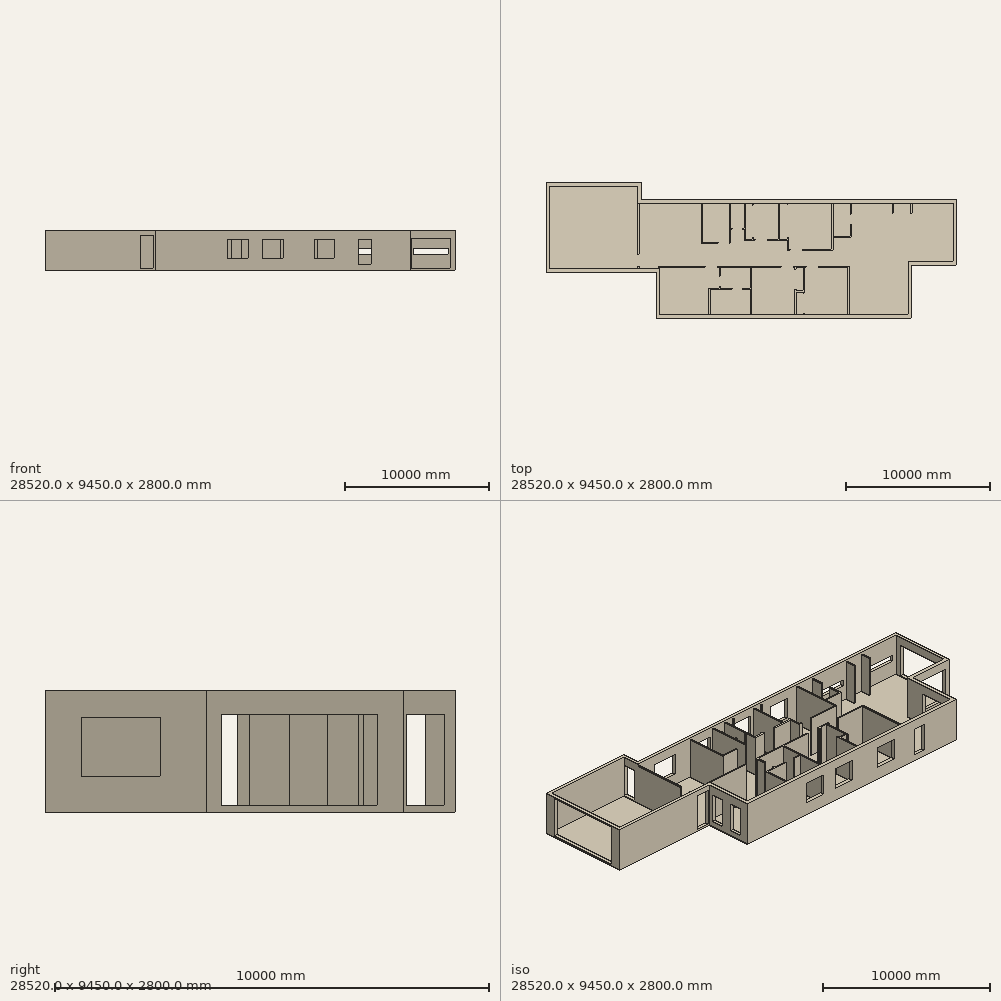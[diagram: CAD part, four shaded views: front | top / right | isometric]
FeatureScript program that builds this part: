
annotation { "Feature Type Name" : "Feature", "Feature Type Description" : "" }
export const myFeature = defineFeature(function(context is Context, id is Id, definition is map)
    precondition{}
    {
        {
            var Q0;
            Q0=qCreatedBy(makeId("Top.planeOp"),FACE);
            var sketch = newSketch(context, id + "F0", { "sketchPlane" : qUnion([Q0])});
            skLineSegment(sketch, "E0.bottom", {"start": v(-9337.55, 6230) * mm, "end": v(-2747.55, 6230) * mm});
            skLineSegment(sketch, "E0.top", {"start": v(-9337.55, 0) * mm, "end": v(-2747.55, 0) * mm});
            skLineSegment(sketch, "E0.left", {"start": v(-9337.55, 6230) * mm, "end": v(-9337.55, 0) * mm});
            skLineSegment(sketch, "E0.right", {"start": v(-2747.55, 6230) * mm, "end": v(-2747.55, 5040) * mm});
            skLineSegment(sketch, "E1.bottom", {"start": v(-2747.55, 5040) * mm, "end": v(19182.45, 5040) * mm});
            skLineSegment(sketch, "E1.top", {"start": v(16062.45, 490) * mm, "end": v(19182.45, 490) * mm});
            skLineSegment(sketch, "E1.right", {"start": v(19182.45, 5040) * mm, "end": v(19182.45, 490) * mm});
            skLineSegment(sketch, "E2.top", {"start": v(-1687.55, -3220) * mm, "end": v(16062.45, -3220) * mm});
            skLineSegment(sketch, "E2.left", {"start": v(-1687.55, 490) * mm, "end": v(-1687.55, -3220) * mm});
            skLineSegment(sketch, "E2.right", {"start": v(16062.45, 490) * mm, "end": v(16062.45, -3220) * mm});
            skLineSegment(sketch, "E3", {"start": v(-2747.55, 0) * mm, "end": v(-1687.55, 0) * mm});
            skLineSegment(sketch, "E4.bottom", {"start": v(19182.45, 5040) * mm, "end": v(22182.45, 5040) * mm});
            skLineSegment(sketch, "E4.top", {"start": v(19182.45, -3220) * mm, "end": v(22182.45, -3220) * mm});
            skLineSegment(sketch, "E4.right", {"start": v(22182.45, 5040) * mm, "end": v(22182.45, -3220) * mm});
            skLineSegment(sketch, "E5.top", {"start": v(16062.45, -3220) * mm, "end": v(19182.45, -3220) * mm});
            skSolve(sketch);
        }
        {
            var Q0;
            Q0=makeQuery(id+"F0.imprint","IMPRINT",FACE,{"disambiguationData":[TD([[makeQuery(id+"F0.imprint","IMPRINT",EDGE,{"derivedFrom":sQuery(id+"F0.wireOp",EDGE,"E0.bottom")}),-1.0]])]});
            extrude(context, id + "F1", {"entities" : qUnion([Q0]), "depth" : 5 * mm});
        }
        {
            var Q0;
            Q0=makeQuery(id+"F1.opExtrude","CAP_FACE",FACE,{"disambiguationData":[OSD([sQuery(id+"F0.wireOp",EDGE,"E0.bottom"),sQuery(id+"F0.wireOp",EDGE,"E0.top"),sQuery(id+"F0.wireOp",EDGE,"E0.left"),sQuery(id+"F0.wireOp",EDGE,"E0.right"),sQuery(id+"F0.wireOp",EDGE,"E1.bottom"),sQuery(id+"F0.wireOp",EDGE,"E2.top"),sQuery(id+"F0.wireOp",EDGE,"E2.left"),sQuery(id+"F0.wireOp",EDGE,"E3"),sQuery(id+"F0.wireOp",EDGE,"E1.right"),sQuery(id+"F0.wireOp",EDGE,"E1.top"),sQuery(id+"F0.wireOp",EDGE,"E2.right")])],"isStart":false});
            var sketch = newSketch(context, id + "F2", { "sketchPlane" : qUnion([Q0])});
            skLineSegment(sketch, "E6.bottom", {"start": v(-9337.55, 6230) * mm, "end": v(-2747.55, 6230) * mm});
            skLineSegment(sketch, "E6.top", {"start": v(-9097.55, 5990) * mm, "end": v(-2987.55, 5990) * mm});
            skLineSegment(sketch, "E6.left", {"start": v(-9337.55, 6230) * mm, "end": v(-9337.55, 5990) * mm});
            skLineSegment(sketch, "E6.right", {"start": v(-2747.55, 6230) * mm, "end": v(-2747.55, 5990) * mm});
            skLineSegment(sketch, "E7.left", {"start": v(-2987.55, 5990) * mm, "end": v(-2987.55, 5040) * mm});
            skLineSegment(sketch, "E7.right", {"start": v(-2747.55, 5990) * mm, "end": v(-2747.55, 5040) * mm});
            skLineSegment(sketch, "E8.bottom", {"start": v(-2747.55, 5040) * mm, "end": v(19182.45, 5040) * mm});
            skLineSegment(sketch, "E8.top", {"start": v(-2987.55, 4800) * mm, "end": v(19182.45, 4800) * mm});
            skLineSegment(sketch, "E8.left", {"start": v(-2987.55, 5040) * mm, "end": v(-2987.55, 4800) * mm});
            skLineSegment(sketch, "E8.right", {"start": v(19182.45, 5040) * mm, "end": v(19182.45, 4800) * mm});
            skLineSegment(sketch, "E9.bottom", {"start": v(18942.45, 4800) * mm, "end": v(19182.45, 4800) * mm});
            skLineSegment(sketch, "E9.top", {"start": v(18942.45, 490) * mm, "end": v(19182.45, 490) * mm});
            skLineSegment(sketch, "E9.left", {"start": v(18942.45, 4800) * mm, "end": v(18942.45, 730) * mm});
            skLineSegment(sketch, "E9.right", {"start": v(19182.45, 4800) * mm, "end": v(19182.45, 490) * mm});
            skLineSegment(sketch, "E10.bottom", {"start": v(16062.45, 490) * mm, "end": v(18942.45, 490) * mm});
            skLineSegment(sketch, "E10.top", {"start": v(16062.45, 730) * mm, "end": v(18942.45, 730) * mm});
            skLineSegment(sketch, "E11.bottom", {"start": v(16062.45, 730) * mm, "end": v(15822.45, 730) * mm});
            skLineSegment(sketch, "E11.top", {"start": v(16062.45, -3220) * mm, "end": v(15822.45, -3220) * mm});
            skLineSegment(sketch, "E11.left", {"start": v(16062.45, 490) * mm, "end": v(16062.45, -3220) * mm});
            skLineSegment(sketch, "E11.right", {"start": v(15822.45, 730) * mm, "end": v(15822.45, -2980) * mm});
            skLineSegment(sketch, "E12.bottom", {"start": v(15822.45, -3220) * mm, "end": v(-1687.55, -3220) * mm});
            skLineSegment(sketch, "E12.top", {"start": v(15822.45, -2980) * mm, "end": v(-1447.55, -2980) * mm});
            skLineSegment(sketch, "E12.right", {"start": v(-1687.55, -3220) * mm, "end": v(-1687.55, -2980) * mm});
            skLineSegment(sketch, "E13.left", {"start": v(-1687.55, -2980) * mm, "end": v(-1687.55, 0) * mm});
            skLineSegment(sketch, "E13.right", {"start": v(-1447.55, -2980) * mm, "end": v(-1447.55, 0) * mm});
            skLineSegment(sketch, "E14.bottom", {"start": v(-1687.55, 0) * mm, "end": v(-9337.55, 0) * mm});
            skLineSegment(sketch, "E14.top", {"start": v(-1447.55, 240) * mm, "end": v(-9097.55, 240) * mm});
            skLineSegment(sketch, "E14.left", {"start": v(-1447.55, 0) * mm, "end": v(-1447.55, 240) * mm});
            skLineSegment(sketch, "E14.right", {"start": v(-9337.55, 0) * mm, "end": v(-9337.55, 240) * mm});
            skLineSegment(sketch, "E15.left", {"start": v(-9337.55, 240) * mm, "end": v(-9337.55, 5990) * mm});
            skLineSegment(sketch, "E15.right", {"start": v(-9097.55, 240) * mm, "end": v(-9097.55, 5990) * mm});
            skSolve(sketch);
        }
        {
            var Q0;
            Q0=makeQuery(id+"F2.imprint","IMPRINT",FACE,{"disambiguationData":[TD([[makeQuery(id+"F2.imprint","IMPRINT",EDGE,{"derivedFrom":sQuery(id+"F2.wireOp",EDGE,"E6.bottom")}),-1.0]])]});
            extrude(context, id + "F3", {"entities" : qUnion([Q0]), "operationType" : NewBodyOperationType.ADD, "depth" : 2700 * mm});
        }
        {
            var Q0;
            Q0=makeQuery(id+"F1.opExtrude","CAP_FACE",FACE,{"disambiguationData":[OSD([sQuery(id+"F0.wireOp",EDGE,"E0.bottom"),sQuery(id+"F0.wireOp",EDGE,"E0.top"),sQuery(id+"F0.wireOp",EDGE,"E0.left"),sQuery(id+"F0.wireOp",EDGE,"E0.right"),sQuery(id+"F0.wireOp",EDGE,"E1.bottom"),sQuery(id+"F0.wireOp",EDGE,"E2.top"),sQuery(id+"F0.wireOp",EDGE,"E2.left"),sQuery(id+"F0.wireOp",EDGE,"E3"),sQuery(id+"F0.wireOp",EDGE,"E1.right"),sQuery(id+"F0.wireOp",EDGE,"E1.top"),sQuery(id+"F0.wireOp",EDGE,"E2.right")])],"isStart":false});
            var sketch = newSketch(context, id + "F4", { "sketchPlane" : qUnion([Q0])});
            skLineSegment(sketch, "E16.bottom", {"start": v(-2987.55, 4800) * mm, "end": v(-2897.55, 4800) * mm});
            skLineSegment(sketch, "E16.top", {"start": v(-2987.55, 1210) * mm, "end": v(-2897.55, 1210) * mm});
            skLineSegment(sketch, "E16.left", {"start": v(-2987.55, 4800) * mm, "end": v(-2987.55, 1210) * mm});
            skLineSegment(sketch, "E16.right", {"start": v(-2897.55, 4800) * mm, "end": v(-2897.55, 1210) * mm});
            skLineSegment(sketch, "E17.bottom", {"start": v(1442.45, 4800) * mm, "end": v(1532.45, 4800) * mm});
            skLineSegment(sketch, "E17.top", {"start": v(1442.45, 2000) * mm, "end": v(1532.45, 2000) * mm});
            skLineSegment(sketch, "E17.left", {"start": v(1442.45, 4800) * mm, "end": v(1442.45, 2000) * mm});
            skLineSegment(sketch, "E17.right", {"start": v(1532.45, 4800) * mm, "end": v(1532.45, 2090) * mm});
            skLineSegment(sketch, "E18.bottom", {"start": v(-2987.55, 240) * mm, "end": v(-2897.55, 240) * mm});
            skLineSegment(sketch, "E18.top", {"start": v(-2987.55, 390) * mm, "end": v(-2897.55, 390) * mm});
            skLineSegment(sketch, "E18.left", {"start": v(-2987.55, 240) * mm, "end": v(-2987.55, 390) * mm});
            skLineSegment(sketch, "E18.right", {"start": v(-2897.55, 240) * mm, "end": v(-2897.55, 390) * mm});
            skLineSegment(sketch, "E19.bottom", {"start": v(3362.45, 4800) * mm, "end": v(3452.45, 4800) * mm});
            skLineSegment(sketch, "E19.top", {"start": v(3362.45, 2000) * mm, "end": v(3452.45, 2000) * mm});
            skLineSegment(sketch, "E19.left", {"start": v(3362.45, 4800) * mm, "end": v(3362.45, 2000) * mm});
            skLineSegment(sketch, "E19.right", {"start": v(3452.45, 4800) * mm, "end": v(3452.45, 3030) * mm});
            skLineSegment(sketch, "E20.bottom", {"start": v(1532.45, 2000) * mm, "end": v(2642.45, 2000) * mm});
            skLineSegment(sketch, "E20.top", {"start": v(1532.45, 2090) * mm, "end": v(2642.45, 2090) * mm});
            skLineSegment(sketch, "E20.right", {"start": v(2642.45, 2000) * mm, "end": v(2642.45, 2090) * mm});
            skLineSegment(sketch, "E21.bottom", {"start": v(4402.45, 4800) * mm, "end": v(4492.45, 4800) * mm});
            skLineSegment(sketch, "E21.left", {"start": v(4402.45, 4800) * mm, "end": v(4402.45, 3030) * mm});
            skLineSegment(sketch, "E21.right", {"start": v(4492.45, 4800) * mm, "end": v(4492.45, 2940) * mm});
            skLineSegment(sketch, "E22.bottom", {"start": v(4402.45, 2940) * mm, "end": v(4287.45, 2940) * mm});
            skLineSegment(sketch, "E22.top", {"start": v(4402.45, 3030) * mm, "end": v(4287.45, 3030) * mm});
            skLineSegment(sketch, "E22.right", {"start": v(4287.45, 2940) * mm, "end": v(4287.45, 3030) * mm});
            skLineSegment(sketch, "E23.bottom", {"start": v(3452.45, 3030) * mm, "end": v(3567.45, 3030) * mm});
            skLineSegment(sketch, "E23.top", {"start": v(3452.45, 2940) * mm, "end": v(3567.45, 2940) * mm});
            skLineSegment(sketch, "E23.right", {"start": v(3567.45, 3030) * mm, "end": v(3567.45, 2940) * mm});
            skLineSegment(sketch, "E24.trimOffspring", {"start": v(3452.45, 2940) * mm, "end": v(3452.45, 2000) * mm});
            skLineSegment(sketch, "E25.bottom", {"start": v(5002.45, 4800) * mm, "end": v(5092.45, 4800) * mm});
            skLineSegment(sketch, "E25.top", {"start": v(5002.45, 4650) * mm, "end": v(5092.45, 4650) * mm});
            skLineSegment(sketch, "E25.left", {"start": v(5002.45, 4800) * mm, "end": v(5002.45, 4650) * mm});
            skLineSegment(sketch, "E25.right", {"start": v(5092.45, 4800) * mm, "end": v(5092.45, 4650) * mm});
            skLineSegment(sketch, "E26.bottom", {"start": v(-1447.55, 240) * mm, "end": v(-1537.55, 240) * mm});
            skLineSegment(sketch, "E26.top", {"start": v(-1447.55, 390) * mm, "end": v(-1537.55, 390) * mm});
            skLineSegment(sketch, "E26.left", {"start": v(-1447.55, 240) * mm, "end": v(-1447.55, 300) * mm});
            skLineSegment(sketch, "E26.right", {"start": v(-1537.55, 240) * mm, "end": v(-1537.55, 390) * mm});
            skLineSegment(sketch, "E27.bottom", {"start": v(-1447.55, 390) * mm, "end": v(1727.45, 390) * mm});
            skLineSegment(sketch, "E27.top", {"start": v(-1447.55, 300) * mm, "end": v(1727.45, 300) * mm});
            skLineSegment(sketch, "E27.right", {"start": v(1727.45, 390) * mm, "end": v(1727.45, 300) * mm});
            skLineSegment(sketch, "E28.bottom", {"start": v(1952.45, -2980) * mm, "end": v(2042.45, -2980) * mm});
            skLineSegment(sketch, "E28.left", {"start": v(1952.45, -2980) * mm, "end": v(1952.45, -1210) * mm});
            skLineSegment(sketch, "E28.right", {"start": v(2042.45, -2980) * mm, "end": v(2042.45, -1210) * mm});
            skLineSegment(sketch, "E29.bottom", {"start": v(4852.45, -2980) * mm, "end": v(4942.45, -2980) * mm});
            skLineSegment(sketch, "E29.top", {"start": v(4852.45, 300) * mm, "end": v(4942.45, 300) * mm});
            skLineSegment(sketch, "E29.left", {"start": v(4852.45, -2980) * mm, "end": v(4852.45, 300) * mm});
            skLineSegment(sketch, "E29.right", {"start": v(4942.45, -2980) * mm, "end": v(4942.45, 300) * mm});
            skLineSegment(sketch, "E30.bottom", {"start": v(2042.45, -1210) * mm, "end": v(3582.45, -1210) * mm});
            skLineSegment(sketch, "E30.top", {"start": v(1952.45, -1120) * mm, "end": v(3582.45, -1120) * mm});
            skLineSegment(sketch, "E30.left", {"start": v(1952.45, -1210) * mm, "end": v(1952.45, -1120) * mm});
            skLineSegment(sketch, "E30.right", {"start": v(3582.45, -1210) * mm, "end": v(3582.45, -1120) * mm});
            skLineSegment(sketch, "E31.bottom", {"start": v(4852.45, -1210) * mm, "end": v(4302.45, -1210) * mm});
            skLineSegment(sketch, "E31.top", {"start": v(4852.45, -1120) * mm, "end": v(4302.45, -1120) * mm});
            skLineSegment(sketch, "E31.left", {"start": v(4852.45, -1210) * mm, "end": v(4852.45, -1120) * mm});
            skLineSegment(sketch, "E31.right", {"start": v(4302.45, -1210) * mm, "end": v(4302.45, -1120) * mm});
            skLineSegment(sketch, "E32.bottom", {"start": v(4942.45, 300) * mm, "end": v(2752.45, 300) * mm});
            skLineSegment(sketch, "E32.top", {"start": v(4942.45, 390) * mm, "end": v(2752.45, 390) * mm});
            skLineSegment(sketch, "E32.left", {"start": v(4942.45, 300) * mm, "end": v(4942.45, 390) * mm});
            skLineSegment(sketch, "E33.bottom", {"start": v(2752.45, 390) * mm, "end": v(2662.45, 390) * mm});
            skLineSegment(sketch, "E33.top", {"start": v(2752.45, -285) * mm, "end": v(2662.45, -285) * mm});
            skLineSegment(sketch, "E33.left", {"start": v(2752.45, 300) * mm, "end": v(2752.45, -285) * mm});
            skLineSegment(sketch, "E33.right", {"start": v(2662.45, 300) * mm, "end": v(2662.45, -285) * mm});
            skLineSegment(sketch, "E34.bottom", {"start": v(2662.45, -1120) * mm, "end": v(2752.45, -1120) * mm});
            skLineSegment(sketch, "E34.top", {"start": v(2662.45, -1005) * mm, "end": v(2752.45, -1005) * mm});
            skLineSegment(sketch, "E34.left", {"start": v(2662.45, -1120) * mm, "end": v(2662.45, -1005) * mm});
            skLineSegment(sketch, "E34.right", {"start": v(2752.45, -1120) * mm, "end": v(2752.45, -1005) * mm});
            skLineSegment(sketch, "E35.bottom", {"start": v(2662.45, 390) * mm, "end": v(2547.45, 390) * mm});
            skLineSegment(sketch, "E35.top", {"start": v(2662.45, 300) * mm, "end": v(2547.45, 300) * mm});
            skLineSegment(sketch, "E35.right", {"start": v(2547.45, 390) * mm, "end": v(2547.45, 300) * mm});
            skLineSegment(sketch, "E36.bottom", {"start": v(7942.45, -2980) * mm, "end": v(8032.45, -2980) * mm});
            skLineSegment(sketch, "E36.top", {"start": v(7942.45, -1180) * mm, "end": v(8032.45, -1180) * mm});
            skLineSegment(sketch, "E36.left", {"start": v(7942.45, -2980) * mm, "end": v(7942.45, -1180) * mm});
            skLineSegment(sketch, "E36.right", {"start": v(8032.45, -2980) * mm, "end": v(8032.45, -1385) * mm});
            skLineSegment(sketch, "E37.bottom", {"start": v(8032.45, -1295) * mm, "end": v(8542.45, -1295) * mm});
            skLineSegment(sketch, "E37.top", {"start": v(8032.45, -1385) * mm, "end": v(8542.45, -1385) * mm});
            skLineSegment(sketch, "E38.bottom", {"start": v(8542.45, -1500) * mm, "end": v(8632.45, -1500) * mm});
            skLineSegment(sketch, "E38.left", {"start": v(8542.45, -1500) * mm, "end": v(8542.45, -1385) * mm});
            skLineSegment(sketch, "E38.right", {"start": v(8632.45, -1500) * mm, "end": v(8632.45, 300) * mm});
            skLineSegment(sketch, "E39.bottom", {"start": v(4942.45, 390) * mm, "end": v(7007.45, 390) * mm});
            skLineSegment(sketch, "E39.top", {"start": v(4942.45, 300) * mm, "end": v(7007.45, 300) * mm});
            skLineSegment(sketch, "E39.left", {"start": v(4942.45, 390) * mm, "end": v(4942.45, 300) * mm});
            skLineSegment(sketch, "E39.right", {"start": v(7007.45, 390) * mm, "end": v(7007.45, 300) * mm});
            skLineSegment(sketch, "E40.bottom", {"start": v(8542.45, 300) * mm, "end": v(8032.45, 300) * mm});
            skLineSegment(sketch, "E40.top", {"start": v(8632.45, 390) * mm, "end": v(7827.45, 390) * mm});
            skLineSegment(sketch, "E40.right", {"start": v(7827.45, 300) * mm, "end": v(7827.45, 390) * mm});
            skLineSegment(sketch, "E41.top", {"start": v(7942.45, 185) * mm, "end": v(8032.45, 185) * mm});
            skLineSegment(sketch, "E41.left", {"start": v(7942.45, 300) * mm, "end": v(7942.45, 185) * mm});
            skLineSegment(sketch, "E41.right", {"start": v(8032.45, 300) * mm, "end": v(8032.45, 185) * mm});
            skLineSegment(sketch, "E42.trimOffspring", {"start": v(7942.45, 300) * mm, "end": v(7827.45, 300) * mm});
            skLineSegment(sketch, "E43.trimOffspring", {"start": v(8542.45, -1295) * mm, "end": v(8542.45, 300) * mm});
            skLineSegment(sketch, "E44.trimOffspring", {"start": v(8032.45, -1295) * mm, "end": v(8032.45, -1180) * mm});
            skLineSegment(sketch, "E45.bottom", {"start": v(8542.45, -2980) * mm, "end": v(8632.45, -2980) * mm});
            skLineSegment(sketch, "E45.top", {"start": v(8542.45, -2865) * mm, "end": v(8632.45, -2865) * mm});
            skLineSegment(sketch, "E45.left", {"start": v(8542.45, -2980) * mm, "end": v(8542.45, -2865) * mm});
            skLineSegment(sketch, "E45.right", {"start": v(8632.45, -2980) * mm, "end": v(8632.45, -2865) * mm});
            skLineSegment(sketch, "E46.bottom", {"start": v(8632.45, 300) * mm, "end": v(8747.45, 300) * mm});
            skLineSegment(sketch, "E46.top", {"start": v(8632.45, 390) * mm, "end": v(8747.45, 390) * mm});
            skLineSegment(sketch, "E46.right", {"start": v(8747.45, 300) * mm, "end": v(8747.45, 390) * mm});
            skLineSegment(sketch, "E47.bottom", {"start": v(11632.45, -2980) * mm, "end": v(11722.45, -2980) * mm});
            skLineSegment(sketch, "E47.left", {"start": v(11632.45, -2980) * mm, "end": v(11632.45, 300) * mm});
            skLineSegment(sketch, "E47.right", {"start": v(11722.45, -2980) * mm, "end": v(11722.45, 300) * mm});
            skLineSegment(sketch, "E48.bottom", {"start": v(11632.45, 300) * mm, "end": v(9567.45, 300) * mm});
            skLineSegment(sketch, "E48.top", {"start": v(11722.45, 390) * mm, "end": v(9567.45, 390) * mm});
            skLineSegment(sketch, "E48.left", {"start": v(11722.45, 300) * mm, "end": v(11722.45, 390) * mm});
            skLineSegment(sketch, "E48.right", {"start": v(9567.45, 300) * mm, "end": v(9567.45, 390) * mm});
            skLineSegment(sketch, "E49.bottom", {"start": v(16002.45, 4800) * mm, "end": v(16092.45, 4800) * mm});
            skLineSegment(sketch, "E49.top", {"start": v(16002.45, 4100) * mm, "end": v(16092.45, 4100) * mm});
            skLineSegment(sketch, "E49.left", {"start": v(16002.45, 4800) * mm, "end": v(16002.45, 4100) * mm});
            skLineSegment(sketch, "E49.right", {"start": v(16092.45, 4800) * mm, "end": v(16092.45, 4100) * mm});
            skLineSegment(sketch, "E50.bottom", {"start": v(14712.45, 4800) * mm, "end": v(14802.45, 4800) * mm});
            skLineSegment(sketch, "E50.top", {"start": v(14712.45, 4100) * mm, "end": v(14802.45, 4100) * mm});
            skLineSegment(sketch, "E50.left", {"start": v(14712.45, 4800) * mm, "end": v(14712.45, 4100) * mm});
            skLineSegment(sketch, "E50.right", {"start": v(14802.45, 4800) * mm, "end": v(14802.45, 4100) * mm});
            skLineSegment(sketch, "E51.bottom", {"start": v(11802.45, 4800) * mm, "end": v(11892.45, 4800) * mm});
            skLineSegment(sketch, "E51.top", {"start": v(11802.45, 4005) * mm, "end": v(11892.45, 4005) * mm});
            skLineSegment(sketch, "E51.left", {"start": v(11802.45, 4800) * mm, "end": v(11802.45, 4005) * mm});
            skLineSegment(sketch, "E51.right", {"start": v(11892.45, 4800) * mm, "end": v(11892.45, 4005) * mm});
            skLineSegment(sketch, "E52.bottom", {"start": v(11802.45, 3285) * mm, "end": v(11892.45, 3285) * mm});
            skLineSegment(sketch, "E52.left", {"start": v(11802.45, 3285) * mm, "end": v(11802.45, 2490) * mm});
            skLineSegment(sketch, "E52.right", {"start": v(11892.45, 3285) * mm, "end": v(11892.45, 2490) * mm});
            skLineSegment(sketch, "E53.bottom", {"start": v(11802.45, 2490) * mm, "end": v(10602.45, 2490) * mm});
            skLineSegment(sketch, "E53.top", {"start": v(11892.45, 2400) * mm, "end": v(10602.45, 2400) * mm});
            skLineSegment(sketch, "E53.left", {"start": v(11892.45, 2490) * mm, "end": v(11892.45, 2400) * mm});
            skLineSegment(sketch, "E54.top", {"start": v(10602.45, 4800) * mm, "end": v(10512.45, 4800) * mm});
            skLineSegment(sketch, "E54.left", {"start": v(10602.45, 1570) * mm, "end": v(10602.45, 2400) * mm});
            skLineSegment(sketch, "E54.right", {"start": v(10512.45, 1570) * mm, "end": v(10512.45, 4800) * mm});
            skLineSegment(sketch, "E55.trimOffspring", {"start": v(10602.45, 2490) * mm, "end": v(10602.45, 4800) * mm});
            skLineSegment(sketch, "E56.bottom", {"start": v(10512.45, 1570) * mm, "end": v(8452.45, 1570) * mm});
            skLineSegment(sketch, "E56.top", {"start": v(10602.45, 1480) * mm, "end": v(8452.45, 1480) * mm});
            skLineSegment(sketch, "E56.left", {"start": v(10602.45, 1570) * mm, "end": v(10602.45, 1480) * mm});
            skLineSegment(sketch, "E56.right", {"start": v(8452.45, 1570) * mm, "end": v(8452.45, 1480) * mm});
            skLineSegment(sketch, "E57.bottom", {"start": v(7482.45, 4800) * mm, "end": v(7392.45, 4800) * mm});
            skLineSegment(sketch, "E57.top", {"start": v(7482.45, 4685) * mm, "end": v(7392.45, 4685) * mm});
            skLineSegment(sketch, "E57.left", {"start": v(7482.45, 4800) * mm, "end": v(7482.45, 4685) * mm});
            skLineSegment(sketch, "E57.right", {"start": v(7392.45, 4800) * mm, "end": v(7392.45, 4685) * mm});
            skLineSegment(sketch, "E58.bottom", {"start": v(7632.45, 1570) * mm, "end": v(7482.45, 1570) * mm});
            skLineSegment(sketch, "E58.top", {"start": v(7632.45, 1480) * mm, "end": v(7482.45, 1480) * mm});
            skLineSegment(sketch, "E58.left", {"start": v(7632.45, 1570) * mm, "end": v(7632.45, 1480) * mm});
            skLineSegment(sketch, "E58.right", {"start": v(7482.45, 1570) * mm, "end": v(7482.45, 1480) * mm});
            skLineSegment(sketch, "E59.bottom", {"start": v(7482.45, 1480) * mm, "end": v(7392.45, 1480) * mm});
            skLineSegment(sketch, "E59.top", {"start": v(7482.45, 2415) * mm, "end": v(7392.45, 2415) * mm});
            skLineSegment(sketch, "E59.left", {"start": v(7482.45, 1480) * mm, "end": v(7482.45, 2415) * mm});
            skLineSegment(sketch, "E59.right", {"start": v(7392.45, 1480) * mm, "end": v(7392.45, 2210) * mm});
            skLineSegment(sketch, "E60.bottom", {"start": v(6882.45, 4800) * mm, "end": v(6792.45, 4800) * mm});
            skLineSegment(sketch, "E60.top", {"start": v(6882.45, 2210) * mm, "end": v(6792.45, 2210) * mm});
            skLineSegment(sketch, "E60.left", {"start": v(6882.45, 4800) * mm, "end": v(6882.45, 2300) * mm});
            skLineSegment(sketch, "E60.right", {"start": v(6792.45, 4800) * mm, "end": v(6792.45, 2300) * mm});
            skLineSegment(sketch, "E61.bottom", {"start": v(6882.45, 2210) * mm, "end": v(7392.45, 2210) * mm});
            skLineSegment(sketch, "E61.top", {"start": v(6882.45, 2300) * mm, "end": v(7392.45, 2300) * mm});
            skLineSegment(sketch, "E62.trimOffspring", {"start": v(7392.45, 2300) * mm, "end": v(7392.45, 2415) * mm});
            skLineSegment(sketch, "E63.bottom", {"start": v(6792.45, 2210) * mm, "end": v(6027.45, 2210) * mm});
            skLineSegment(sketch, "E63.top", {"start": v(6792.45, 2300) * mm, "end": v(6027.45, 2300) * mm});
            skLineSegment(sketch, "E63.right", {"start": v(6027.45, 2210) * mm, "end": v(6027.45, 2300) * mm});
            skLineSegment(sketch, "E64.top", {"start": v(4402.45, 2210) * mm, "end": v(4492.45, 2210) * mm});
            skLineSegment(sketch, "E64.left", {"start": v(4402.45, 2940) * mm, "end": v(4402.45, 2210) * mm});
            skLineSegment(sketch, "E64.right", {"start": v(4492.45, 2940) * mm, "end": v(4492.45, 2300) * mm});
            skLineSegment(sketch, "E65.bottom", {"start": v(4492.45, 2210) * mm, "end": v(5207.45, 2210) * mm});
            skLineSegment(sketch, "E65.top", {"start": v(4492.45, 2300) * mm, "end": v(5002.45, 2300) * mm});
            skLineSegment(sketch, "E65.right", {"start": v(5207.45, 2210) * mm, "end": v(5207.45, 2300) * mm});
            skPoint(sketch, "E66.oppositeSnap0", {"position": v(5092.45, 4725) * mm});
            skLineSegment(sketch, "E66.top", {"start": v(5002.45, 2415) * mm, "end": v(5092.45, 2415) * mm});
            skLineSegment(sketch, "E66.left", {"start": v(5002.45, 2300) * mm, "end": v(5002.45, 2415) * mm});
            skLineSegment(sketch, "E66.right", {"start": v(5092.45, 2300) * mm, "end": v(5092.45, 2415) * mm});
            skLineSegment(sketch, "E67.trimOffspring", {"start": v(5092.45, 2300) * mm, "end": v(5207.45, 2300) * mm});
            skSolve(sketch);
        }
        {
            var Q0;
            Q0 = qSketchRegion(id + "F4", true);
            extrude(context, id + "F5", {"entities" : qUnion([Q0]), "operationType" : NewBodyOperationType.ADD, "depth" : 2590 * mm});
        }
        {
            var Q0;
            Q0=makeQuery(id+"F3.boolean.opBoolean","MERGE",FACE,{"derivedFrom":[makeQuery(id+"F1.opExtrude","SWEPT_FACE",FACE,{"disambiguationData":[OSD([sQuery(id+"F0.wireOp",EDGE,"E0.left")])]}),makeQuery(id+"F3.opExtrude","SWEPT_FACE",FACE,{"disambiguationData":[OSD([sQuery(id+"F2.wireOp",EDGE,"E6.left"),sQuery(id+"F2.wireOp",EDGE,"E14.right"),sQuery(id+"F2.wireOp",EDGE,"E15.left")])]})]});
            var sketch = newSketch(context, id + "F6", { "sketchPlane" : qUnion([Q0])});
            skLineSegment(sketch, "E68.bottom", {"start": v(-5530, 2620) * mm, "end": v(-700, 2620) * mm});
            skLineSegment(sketch, "E68.top", {"start": v(-5530, 30) * mm, "end": v(-700, 30) * mm});
            skLineSegment(sketch, "E68.left", {"start": v(-5530, 2620) * mm, "end": v(-5530, 30) * mm});
            skLineSegment(sketch, "E68.right", {"start": v(-700, 2620) * mm, "end": v(-700, 30) * mm});
            skSolve(sketch);
        }
        {
            var Q0;
            Q0=makeQuery(id+"F6.imprint","IMPRINT",FACE,{"disambiguationData":[TD([[makeQuery(id+"F6.imprint","IMPRINT",EDGE,{"derivedFrom":sQuery(id+"F6.wireOp",EDGE,"E68.bottom")}),-1.0]])]});
            extrude(context, id + "F7", {"entities" : qUnion([Q0]), "operationType" : NewBodyOperationType.REMOVE, "oppositeDirection" : true, "depth" : 400 * mm});
        }
        {
            var Q0;
            Q0=makeQuery(id+"F3.boolean.opBoolean","MERGE",FACE,{"derivedFrom":[makeQuery(id+"F1.opExtrude","SWEPT_FACE",FACE,{"disambiguationData":[OSD([sQuery(id+"F0.wireOp",EDGE,"E0.top"),sQuery(id+"F0.wireOp",EDGE,"E3")])]}),makeQuery(id+"F3.opExtrude","SWEPT_FACE",FACE,{"disambiguationData":[OSD([sQuery(id+"F2.wireOp",EDGE,"E14.bottom")])]})]});
            var sketch = newSketch(context, id + "F8", { "sketchPlane" : qUnion([Q0])});
            skLineSegment(sketch, "E69.bottom", {"start": v(-2722.55, 2370) * mm, "end": v(-1802.55, 2370) * mm});
            skLineSegment(sketch, "E69.top", {"start": v(-2722.55, 30) * mm, "end": v(-1802.55, 30) * mm});
            skLineSegment(sketch, "E69.left", {"start": v(-2722.55, 2370) * mm, "end": v(-2722.55, 30) * mm});
            skLineSegment(sketch, "E69.right", {"start": v(-1802.55, 2370) * mm, "end": v(-1802.55, 30) * mm});
            skSolve(sketch);
        }
        {
            var Q0;
            Q0=makeQuery(id+"F8.imprint","IMPRINT",FACE,{"disambiguationData":[TD([[makeQuery(id+"F8.imprint","IMPRINT",EDGE,{"derivedFrom":sQuery(id+"F8.wireOp",EDGE,"E69.bottom")}),-1.0]])]});
            extrude(context, id + "F9", {"entities" : qUnion([Q0]), "operationType" : NewBodyOperationType.REMOVE, "oppositeDirection" : true, "depth" : 400 * mm});
        }
        {
            var Q0;
            Q0=makeQuery(id+"F3.boolean.opBoolean","MERGE",FACE,{"derivedFrom":[makeQuery(id+"F1.opExtrude","SWEPT_FACE",FACE,{"disambiguationData":[OSD([sQuery(id+"F0.wireOp",EDGE,"E2.left")])]}),makeQuery(id+"F3.opExtrude","SWEPT_FACE",FACE,{"disambiguationData":[OSD([sQuery(id+"F2.wireOp",EDGE,"E12.right"),sQuery(id+"F2.wireOp",EDGE,"E13.left")])]})]});
            var sketch = newSketch(context, id + "F10", { "sketchPlane" : qUnion([Q0])});
            skLineSegment(sketch, "E70.bottom", {"start": v(1780, 2100) * mm, "end": v(2630, 2100) * mm});
            skLineSegment(sketch, "E70.top", {"start": v(1780, 260) * mm, "end": v(2630, 260) * mm});
            skLineSegment(sketch, "E70.left", {"start": v(1780, 2100) * mm, "end": v(1780, 260) * mm});
            skLineSegment(sketch, "E70.right", {"start": v(2630, 2100) * mm, "end": v(2630, 260) * mm});
            skLineSegment(sketch, "E71.bottom", {"start": v(1070, 2100) * mm, "end": v(220, 2100) * mm});
            skLineSegment(sketch, "E71.top", {"start": v(1070, 260) * mm, "end": v(220, 260) * mm});
            skLineSegment(sketch, "E71.left", {"start": v(1070, 2100) * mm, "end": v(1070, 260) * mm});
            skLineSegment(sketch, "E71.right", {"start": v(220, 2100) * mm, "end": v(220, 260) * mm});
            skSolve(sketch);
        }
        {
            var Q0;
            Q0=makeQuery(id+"F10.imprint","IMPRINT",FACE,{"disambiguationData":[TD([[makeQuery(id+"F10.imprint","IMPRINT",EDGE,{"derivedFrom":sQuery(id+"F10.wireOp",EDGE,"E71.bottom")}),1.0]])]});
            var Q1;
            Q1=makeQuery(id+"F10.imprint","IMPRINT",FACE,{"disambiguationData":[TD([[makeQuery(id+"F10.imprint","IMPRINT",EDGE,{"derivedFrom":sQuery(id+"F10.wireOp",EDGE,"E70.bottom")}),-1.0]])]});
            extrude(context, id + "F11", {"entities" : qUnion([Q0, Q1]), "operationType" : NewBodyOperationType.REMOVE, "oppositeDirection" : true, "depth" : 350 * mm});
        }
        {
            var Q0;
            Q0=makeQuery(id+"F3.boolean.opBoolean","MERGE",FACE,{"derivedFrom":[makeQuery(id+"F1.opExtrude","SWEPT_FACE",FACE,{"disambiguationData":[OSD([sQuery(id+"F0.wireOp",EDGE,"E2.top")])]}),makeQuery(id+"F3.opExtrude","SWEPT_FACE",FACE,{"disambiguationData":[OSD([sQuery(id+"F2.wireOp",EDGE,"E11.top"),sQuery(id+"F2.wireOp",EDGE,"E12.bottom")])]})]});
            var sketch = newSketch(context, id + "F12", { "sketchPlane" : qUnion([Q0])});
            skLineSegment(sketch, "E72.bottom", {"start": v(3342.45, 2100) * mm, "end": v(4792.45, 2100) * mm});
            skLineSegment(sketch, "E72.top", {"start": v(3342.45, 728) * mm, "end": v(4792.45, 728) * mm});
            skLineSegment(sketch, "E72.left", {"start": v(3342.45, 2100) * mm, "end": v(3342.45, 728) * mm});
            skLineSegment(sketch, "E72.right", {"start": v(4792.45, 2100) * mm, "end": v(4792.45, 728) * mm});
            skLineSegment(sketch, "E73.bottom", {"start": v(5742.45, 728) * mm, "end": v(7192.45, 728) * mm});
            skLineSegment(sketch, "E73.top", {"start": v(5742.45, 2100) * mm, "end": v(7192.45, 2100) * mm});
            skLineSegment(sketch, "E73.left", {"start": v(5742.45, 728) * mm, "end": v(5742.45, 2100) * mm});
            skLineSegment(sketch, "E73.right", {"start": v(7192.45, 728) * mm, "end": v(7192.45, 2100) * mm});
            skLineSegment(sketch, "E74.bottom", {"start": v(10792.45, 2100) * mm, "end": v(9342.45, 2100) * mm});
            skLineSegment(sketch, "E74.top", {"start": v(10792.45, 728) * mm, "end": v(9342.45, 728) * mm});
            skLineSegment(sketch, "E74.left", {"start": v(10792.45, 2100) * mm, "end": v(10792.45, 728) * mm});
            skLineSegment(sketch, "E74.right", {"start": v(9342.45, 2100) * mm, "end": v(9342.45, 728) * mm});
            skLineSegment(sketch, "E75.bottom", {"start": v(12462.45, 300) * mm, "end": v(13312.45, 300) * mm});
            skLineSegment(sketch, "E75.top", {"start": v(12462.45, 2100) * mm, "end": v(13312.45, 2100) * mm});
            skLineSegment(sketch, "E75.left", {"start": v(12462.45, 300) * mm, "end": v(12462.45, 2100) * mm});
            skLineSegment(sketch, "E75.right", {"start": v(13312.45, 300) * mm, "end": v(13312.45, 2100) * mm});
            skSolve(sketch);
        }
        {
            var Q0;
            Q0=makeQuery(id+"F12.imprint","IMPRINT",FACE,{"disambiguationData":[TD([[makeQuery(id+"F12.imprint","IMPRINT",EDGE,{"derivedFrom":sQuery(id+"F12.wireOp",EDGE,"E72.bottom")}),-1.0]])]});
            var Q1;
            Q1=makeQuery(id+"F12.imprint","IMPRINT",FACE,{"disambiguationData":[TD([[makeQuery(id+"F12.imprint","IMPRINT",EDGE,{"derivedFrom":sQuery(id+"F12.wireOp",EDGE,"E73.bottom")}),1.0]])]});
            var Q2;
            Q2=makeQuery(id+"F12.imprint","IMPRINT",FACE,{"disambiguationData":[TD([[makeQuery(id+"F12.imprint","IMPRINT",EDGE,{"derivedFrom":sQuery(id+"F12.wireOp",EDGE,"E74.bottom")}),1.0]])]});
            var Q3;
            Q3=makeQuery(id+"F12.imprint","IMPRINT",FACE,{"disambiguationData":[TD([[makeQuery(id+"F12.imprint","IMPRINT",EDGE,{"derivedFrom":sQuery(id+"F12.wireOp",EDGE,"E75.bottom")}),1.0]])]});
            extrude(context, id + "F13", {"entities" : qUnion([Q0, Q1, Q2, Q3]), "operationType" : NewBodyOperationType.REMOVE, "oppositeDirection" : true, "depth" : 400 * mm});
        }
        {
            var Q0;
            Q0=makeQuery(id+"F3.boolean.opBoolean","MERGE",FACE,{"derivedFrom":[makeQuery(id+"F1.opExtrude","SWEPT_FACE",FACE,{"disambiguationData":[OSD([sQuery(id+"F0.wireOp",EDGE,"E1.top")])]}),makeQuery(id+"F3.opExtrude","SWEPT_FACE",FACE,{"disambiguationData":[OSD([sQuery(id+"F2.wireOp",EDGE,"E9.top"),sQuery(id+"F2.wireOp",EDGE,"E10.bottom")])]})]});
            var sketch = newSketch(context, id + "F14", { "sketchPlane" : qUnion([Q0])});
            skLineSegment(sketch, "E76.bottom", {"start": v(16144.45, 2160) * mm, "end": v(18832.45, 2160) * mm});
            skLineSegment(sketch, "E76.top", {"start": v(16144.45, 50) * mm, "end": v(18832.45, 50) * mm});
            skLineSegment(sketch, "E76.left", {"start": v(16144.45, 2160) * mm, "end": v(16144.45, 50) * mm});
            skLineSegment(sketch, "E76.right", {"start": v(18832.45, 2160) * mm, "end": v(18832.45, 50) * mm});
            skSolve(sketch);
        }
        {
            var Q0;
            Q0=makeQuery(id+"F14.imprint","IMPRINT",FACE,{"disambiguationData":[TD([[makeQuery(id+"F14.imprint","IMPRINT",EDGE,{"derivedFrom":sQuery(id+"F14.wireOp",EDGE,"E76.bottom")}),-1.0]])]});
            extrude(context, id + "F15", {"entities" : qUnion([Q0]), "operationType" : NewBodyOperationType.REMOVE, "oppositeDirection" : true, "depth" : 350 * mm});
        }
        {
            var Q0;
            Q0=makeQuery(id+"F3.boolean.opBoolean","MERGE",FACE,{"derivedFrom":[makeQuery(id+"F1.opExtrude","SWEPT_FACE",FACE,{"disambiguationData":[OSD([sQuery(id+"F0.wireOp",EDGE,"E2.right")])]}),makeQuery(id+"F3.opExtrude","SWEPT_FACE",FACE,{"disambiguationData":[OSD([sQuery(id+"F2.wireOp",EDGE,"E11.left")])]})]});
            var sketch = newSketch(context, id + "F16", { "sketchPlane" : qUnion([Q0])});
            skLineSegment(sketch, "E77.bottom", {"start": v(-2390, 2100) * mm, "end": v(-570, 2100) * mm});
            skLineSegment(sketch, "E77.top", {"start": v(-2390, 728) * mm, "end": v(-570, 728) * mm});
            skLineSegment(sketch, "E77.left", {"start": v(-2390, 2100) * mm, "end": v(-2390, 728) * mm});
            skLineSegment(sketch, "E77.right", {"start": v(-570, 2100) * mm, "end": v(-570, 728) * mm});
            skSolve(sketch);
        }
        {
            var Q0;
            Q0=makeQuery(id+"F16.imprint","IMPRINT",FACE,{"disambiguationData":[TD([[makeQuery(id+"F16.imprint","IMPRINT",EDGE,{"derivedFrom":sQuery(id+"F16.wireOp",EDGE,"E77.bottom")}),-1.0]])]});
            extrude(context, id + "F17", {"entities" : qUnion([Q0]), "operationType" : NewBodyOperationType.REMOVE, "oppositeDirection" : true, "depth" : 400 * mm});
        }
        {
            var Q0;
            Q0=makeQuery(id+"F3.boolean.opBoolean","MERGE",FACE,{"derivedFrom":[makeQuery(id+"F1.opExtrude","SWEPT_FACE",FACE,{"disambiguationData":[OSD([sQuery(id+"F0.wireOp",EDGE,"E1.right")])]}),makeQuery(id+"F3.opExtrude","SWEPT_FACE",FACE,{"disambiguationData":[OSD([sQuery(id+"F2.wireOp",EDGE,"E8.right"),sQuery(id+"F2.wireOp",EDGE,"E9.right")])]})]});
            var sketch = newSketch(context, id + "F18", { "sketchPlane" : qUnion([Q0])});
            skLineSegment(sketch, "E78.bottom", {"start": v(840, 2160) * mm, "end": v(4428, 2160) * mm});
            skLineSegment(sketch, "E78.top", {"start": v(840, 50) * mm, "end": v(4428, 50) * mm});
            skLineSegment(sketch, "E78.left", {"start": v(840, 2160) * mm, "end": v(840, 50) * mm});
            skLineSegment(sketch, "E78.right", {"start": v(4428, 2160) * mm, "end": v(4428, 50) * mm});
            skSolve(sketch);
        }
        {
            var Q0;
            Q0=makeQuery(id+"F18.imprint","IMPRINT",FACE,{"disambiguationData":[TD([[makeQuery(id+"F18.imprint","IMPRINT",EDGE,{"derivedFrom":sQuery(id+"F18.wireOp",EDGE,"E78.bottom")}),-1.0]])]});
            extrude(context, id + "F19", {"entities" : qUnion([Q0]), "operationType" : NewBodyOperationType.REMOVE, "oppositeDirection" : true, "depth" : 400 * mm});
        }
        {
            var Q0;
            Q0=makeQuery(id+"F3.boolean.opBoolean","MERGE",FACE,{"derivedFrom":[makeQuery(id+"F1.opExtrude","SWEPT_FACE",FACE,{"disambiguationData":[OSD([sQuery(id+"F0.wireOp",EDGE,"E0.right")])]}),makeQuery(id+"F3.opExtrude","SWEPT_FACE",FACE,{"disambiguationData":[OSD([sQuery(id+"F2.wireOp",EDGE,"E6.right"),sQuery(id+"F2.wireOp",EDGE,"E7.right")])]})]});
            var sketch = newSketch(context, id + "F20", { "sketchPlane" : qUnion([Q0])});
            skLineSegment(sketch, "E79.bottom", {"start": v(5090, 2160) * mm, "end": v(5975, 2160) * mm});
            skLineSegment(sketch, "E79.top", {"start": v(5090, 55) * mm, "end": v(5975, 55) * mm});
            skLineSegment(sketch, "E79.left", {"start": v(5090, 2160) * mm, "end": v(5090, 55) * mm});
            skLineSegment(sketch, "E79.right", {"start": v(5975, 2160) * mm, "end": v(5975, 55) * mm});
            skSolve(sketch);
        }
        {
            var Q0;
            Q0=makeQuery(id+"F20.imprint","IMPRINT",FACE,{"disambiguationData":[TD([[makeQuery(id+"F20.imprint","IMPRINT",EDGE,{"derivedFrom":sQuery(id+"F20.wireOp",EDGE,"E79.bottom")}),-1.0]])]});
            extrude(context, id + "F21", {"entities" : qUnion([Q0]), "operationType" : NewBodyOperationType.REMOVE, "oppositeDirection" : true, "depth" : 400 * mm});
        }
        {
            var Q0;
            Q0=makeQuery(id+"F3.boolean.opBoolean","MERGE",FACE,{"derivedFrom":[makeQuery(id+"F1.opExtrude","SWEPT_FACE",FACE,{"disambiguationData":[OSD([sQuery(id+"F0.wireOp",EDGE,"E1.bottom")])]}),makeQuery(id+"F3.opExtrude","SWEPT_FACE",FACE,{"disambiguationData":[OSD([sQuery(id+"F2.wireOp",EDGE,"E8.bottom")])]})]});
            var sketch = newSketch(context, id + "F22", { "sketchPlane" : qUnion([Q0])});
            skLineSegment(sketch, "E80.bottom", {"start": v(-18682.45, 1425) * mm, "end": v(-16272.45, 1425) * mm});
            skLineSegment(sketch, "E80.top", {"start": v(-18682.45, 1005) * mm, "end": v(-16272.45, 1005) * mm});
            skLineSegment(sketch, "E80.left", {"start": v(-18682.45, 1425) * mm, "end": v(-18682.45, 1005) * mm});
            skLineSegment(sketch, "E80.right", {"start": v(-16272.45, 1425) * mm, "end": v(-16272.45, 1005) * mm});
            skLineSegment(sketch, "E81.bottom", {"start": v(-14482.45, 1425) * mm, "end": v(-12072.45, 1425) * mm});
            skLineSegment(sketch, "E81.top", {"start": v(-14482.45, 1005) * mm, "end": v(-12072.45, 1005) * mm});
            skLineSegment(sketch, "E81.left", {"start": v(-14482.45, 1425) * mm, "end": v(-14482.45, 1005) * mm});
            skLineSegment(sketch, "E81.right", {"start": v(-12072.45, 1425) * mm, "end": v(-12072.45, 1005) * mm});
            skLineSegment(sketch, "E82.bottom", {"start": v(-9682.45, 2100) * mm, "end": v(-8232.45, 2100) * mm});
            skLineSegment(sketch, "E82.top", {"start": v(-9682.45, 728) * mm, "end": v(-8232.45, 728) * mm});
            skLineSegment(sketch, "E82.left", {"start": v(-9682.45, 2100) * mm, "end": v(-9682.45, 728) * mm});
            skLineSegment(sketch, "E82.right", {"start": v(-8232.45, 2100) * mm, "end": v(-8232.45, 728) * mm});
            skLineSegment(sketch, "E83.bottom", {"start": v(-6612.45, 2160) * mm, "end": v(-5162.45, 2160) * mm});
            skLineSegment(sketch, "E83.top", {"start": v(-6612.45, 60) * mm, "end": v(-5162.45, 60) * mm});
            skLineSegment(sketch, "E83.left", {"start": v(-6612.45, 2160) * mm, "end": v(-6612.45, 60) * mm});
            skLineSegment(sketch, "E83.right", {"start": v(-5162.45, 2160) * mm, "end": v(-5162.45, 60) * mm});
            skLineSegment(sketch, "E84.bottom", {"start": v(-4232.45, 2100) * mm, "end": v(-3622.45, 2100) * mm});
            skLineSegment(sketch, "E84.top", {"start": v(-4232.45, 1243) * mm, "end": v(-3622.45, 1243) * mm});
            skLineSegment(sketch, "E84.left", {"start": v(-4232.45, 2100) * mm, "end": v(-4232.45, 1243) * mm});
            skLineSegment(sketch, "E84.right", {"start": v(-3622.45, 2100) * mm, "end": v(-3622.45, 1243) * mm});
            skLineSegment(sketch, "E85.bottom", {"start": v(-3152.45, 2100) * mm, "end": v(-1702.45, 2100) * mm});
            skLineSegment(sketch, "E85.top", {"start": v(-3152.45, 728) * mm, "end": v(-1702.45, 728) * mm});
            skLineSegment(sketch, "E85.left", {"start": v(-3152.45, 2100) * mm, "end": v(-3152.45, 728) * mm});
            skLineSegment(sketch, "E85.right", {"start": v(-1702.45, 2100) * mm, "end": v(-1702.45, 728) * mm});
            skLineSegment(sketch, "E86.bottom", {"start": v(-192.45, 2100) * mm, "end": v(1617.55, 2100) * mm});
            skLineSegment(sketch, "E86.top", {"start": v(-192.45, 728) * mm, "end": v(1617.55, 728) * mm});
            skLineSegment(sketch, "E86.left", {"start": v(-192.45, 2100) * mm, "end": v(-192.45, 728) * mm});
            skLineSegment(sketch, "E86.right", {"start": v(1617.55, 2100) * mm, "end": v(1617.55, 728) * mm});
            skSolve(sketch);
        }
        {
            var Q0;
            Q0=makeQuery(id+"F22.imprint","IMPRINT",FACE,{"disambiguationData":[TD([[makeQuery(id+"F22.imprint","IMPRINT",EDGE,{"derivedFrom":sQuery(id+"F22.wireOp",EDGE,"E80.bottom")}),-1.0]])]});
            var Q1;
            Q1=makeQuery(id+"F22.imprint","IMPRINT",FACE,{"disambiguationData":[TD([[makeQuery(id+"F22.imprint","IMPRINT",EDGE,{"derivedFrom":sQuery(id+"F22.wireOp",EDGE,"E81.bottom")}),-1.0]])]});
            var Q2;
            Q2=makeQuery(id+"F22.imprint","IMPRINT",FACE,{"disambiguationData":[TD([[makeQuery(id+"F22.imprint","IMPRINT",EDGE,{"derivedFrom":sQuery(id+"F22.wireOp",EDGE,"E82.bottom")}),-1.0]])]});
            var Q3;
            Q3=makeQuery(id+"F22.imprint","IMPRINT",FACE,{"disambiguationData":[TD([[makeQuery(id+"F22.imprint","IMPRINT",EDGE,{"derivedFrom":sQuery(id+"F22.wireOp",EDGE,"E83.bottom")}),-1.0]])]});
            var Q4;
            Q4=makeQuery(id+"F22.imprint","IMPRINT",FACE,{"disambiguationData":[TD([[makeQuery(id+"F22.imprint","IMPRINT",EDGE,{"derivedFrom":sQuery(id+"F22.wireOp",EDGE,"E84.bottom")}),-1.0]])]});
            var Q5;
            Q5=makeQuery(id+"F22.imprint","IMPRINT",FACE,{"disambiguationData":[TD([[makeQuery(id+"F22.imprint","IMPRINT",EDGE,{"derivedFrom":sQuery(id+"F22.wireOp",EDGE,"E85.bottom")}),-1.0]])]});
            var Q6;
            Q6=makeQuery(id+"F22.imprint","IMPRINT",FACE,{"disambiguationData":[TD([[makeQuery(id+"F22.imprint","IMPRINT",EDGE,{"derivedFrom":sQuery(id+"F22.wireOp",EDGE,"E86.bottom")}),-1.0]])]});
            extrude(context, id + "F23", {"entities" : qUnion([Q0, Q1, Q2, Q3, Q4, Q5, Q6]), "operationType" : NewBodyOperationType.REMOVE, "oppositeDirection" : true, "depth" : 400 * mm});
        }
        {
            var Q0;
            Q0=makeQuery(id+"F1.opExtrude","CAP_FACE",FACE,{"disambiguationData":[OSD([sQuery(id+"F0.wireOp",EDGE,"E0.bottom"),sQuery(id+"F0.wireOp",EDGE,"E0.top"),sQuery(id+"F0.wireOp",EDGE,"E0.left"),sQuery(id+"F0.wireOp",EDGE,"E0.right"),sQuery(id+"F0.wireOp",EDGE,"E1.bottom"),sQuery(id+"F0.wireOp",EDGE,"E2.top"),sQuery(id+"F0.wireOp",EDGE,"E2.left"),sQuery(id+"F0.wireOp",EDGE,"E3"),sQuery(id+"F0.wireOp",EDGE,"E1.right"),sQuery(id+"F0.wireOp",EDGE,"E1.top"),sQuery(id+"F0.wireOp",EDGE,"E2.right")])],"isStart":true});
            extrude(context, id + "F24", {"entities" : qUnion([Q0]), "operationType" : NewBodyOperationType.ADD, "depth" : 95 * mm});
        }
    });
